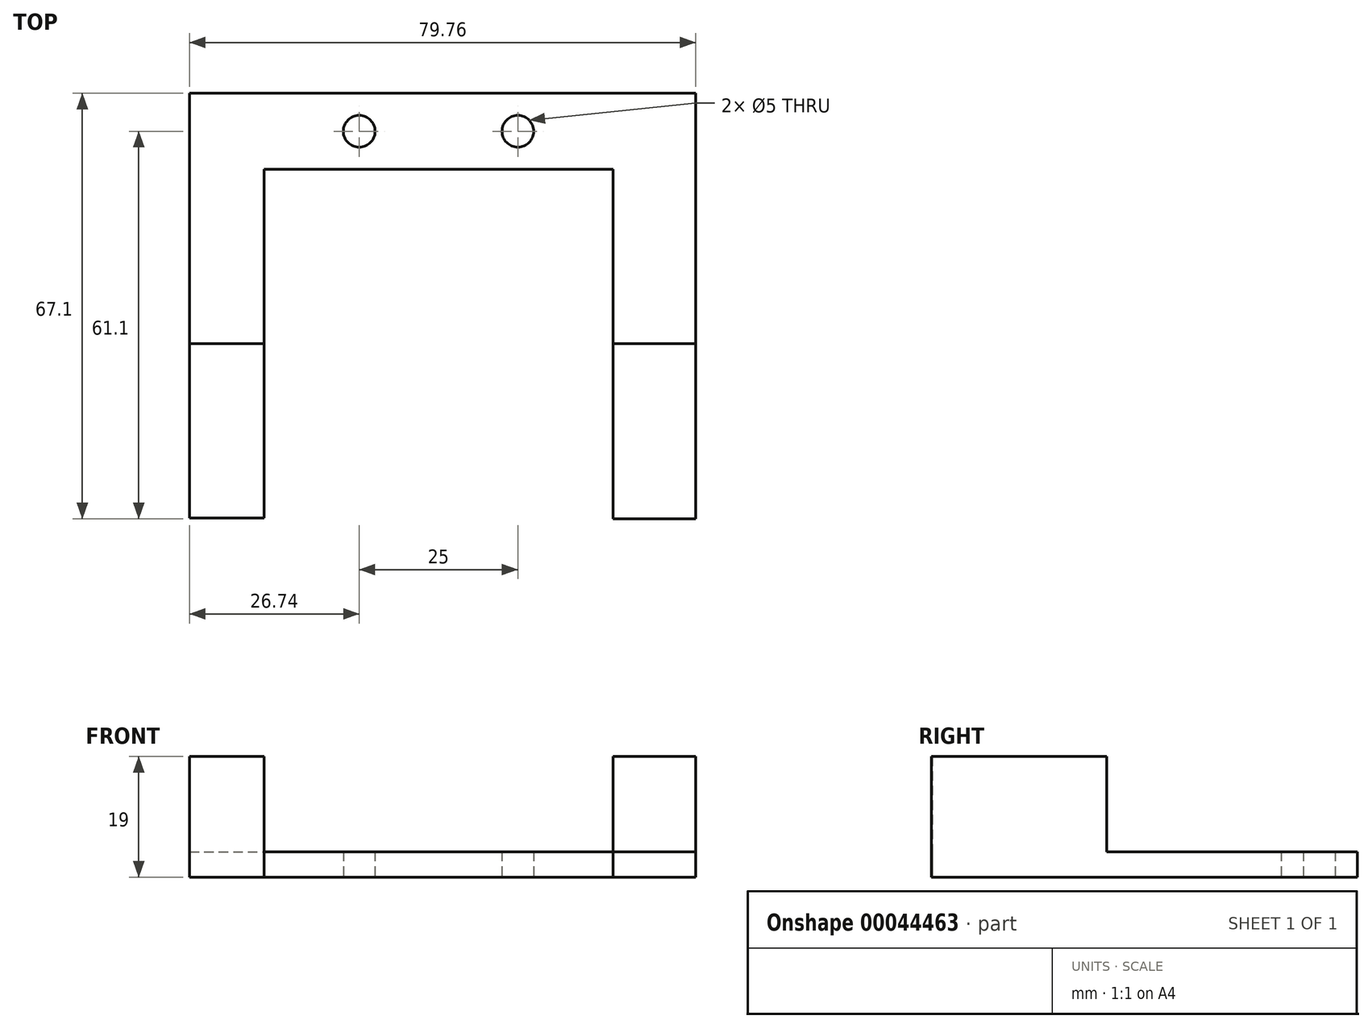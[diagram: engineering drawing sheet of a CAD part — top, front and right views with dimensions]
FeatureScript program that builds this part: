
annotation { "Feature Type Name" : "Feature", "Feature Type Description" : "" }
export const myFeature = defineFeature(function(context is Context, id is Id, definition is map)
    precondition{}
    {
        {
            var Q0;
            Q0=qCreatedBy(makeId("Top.planeOp"),FACE);
            var sketch = newSketch(context, id + "F0", { "sketchPlane" : qUnion([Q0])});
            skLineSegment(sketch, "E0.rect.bottom", {"start": v(27.5, -27.5) * mm, "end": v(-27.5, -27.5) * mm, "construction": true});
            skLineSegment(sketch, "E0.rect.top", {"start": v(27.5, 27.5) * mm, "end": v(-27.5, 27.5) * mm});
            skLineSegment(sketch, "E0.rect.left", {"start": v(27.5, -27.5) * mm, "end": v(27.5, 27.5) * mm});
            skLineSegment(sketch, "E0.rect.right", {"start": v(-27.5, -27.5) * mm, "end": v(-27.5, 27.5) * mm});
            skPoint(sketch, "E0.rect.middle", {"position": v(0, 0) * mm});
            skLineSegment(sketch, "E1", {"start": v(-27.5, -27.5) * mm, "end": v(-39.24, -27.5) * mm});
            skLineSegment(sketch, "E2", {"start": v(-39.24, -27.5) * mm, "end": v(-39.24, 39.5) * mm});
            skLineSegment(sketch, "E3", {"start": v(-39.24, 39.5) * mm, "end": v(40.52, 39.5) * mm});
            skLineSegment(sketch, "E4", {"start": v(40.52, 39.5) * mm, "end": v(40.52, -27.6) * mm});
            skLineSegment(sketch, "E5", {"start": v(27.5, -27.5) * mm, "end": v(40.52, -27.6) * mm});
            skLineSegment(sketch, "E6", {"start": v(-12.5, 0) * mm, "end": v(0, 0) * mm, "construction": true});
            skLineSegment(sketch, "E7", {"start": v(0, 0) * mm, "end": v(12.5, 0) * mm, "construction": true});
            skLineSegment(sketch, "E8", {"start": v(-27.5, 27.5) * mm, "end": v(-27.5, 39.5) * mm, "construction": true});
            skLineSegment(sketch, "E9", {"start": v(-27.5, 33.5) * mm, "end": v(27.8, 33.5) * mm, "construction": true});
            skLineSegment(sketch, "E10", {"start": v(-12.5, 0) * mm, "end": v(-12.5, 33.5) * mm, "construction": true});
            skLineSegment(sketch, "E11", {"start": v(12.5, 0) * mm, "end": v(12.5, 33.5) * mm, "construction": true});
            skCircle(sketch, "E12", {"center": v(-12.5, 33.5) * mm, "radius": 2.5 * mm});
            skCircle(sketch, "E13", {"center": v(12.5, 33.5) * mm, "radius": 2.5 * mm});
            skSolve(sketch);
        }
        {
            var Q0;
            Q0=makeQuery(id+"F0.imprint","IMPRINT",FACE,{"disambiguationData":[TD([[makeQuery(id+"F0.imprint","IMPRINT",EDGE,{"derivedFrom":sQuery(id+"F0.wireOp",EDGE,"E0.rect.top")}),-1.0]])]});
            extrude(context, id + "F1", {"entities" : qUnion([Q0]), "depth" : 4 * mm});
        }
        {
            var Q0;
            Q0=makeQuery(id+"F1.opExtrude","CAP_FACE",FACE,{"disambiguationData":[OSD([sQuery(id+"F0.wireOp",EDGE,"E0.rect.top"),sQuery(id+"F0.wireOp",EDGE,"E0.rect.left"),sQuery(id+"F0.wireOp",EDGE,"E0.rect.right"),sQuery(id+"F0.wireOp",EDGE,"E1"),sQuery(id+"F0.wireOp",EDGE,"E2"),sQuery(id+"F0.wireOp",EDGE,"E3"),sQuery(id+"F0.wireOp",EDGE,"E4"),sQuery(id+"F0.wireOp",EDGE,"E5"),sQuery(id+"F0.wireOp",EDGE,"E12"),sQuery(id+"F0.wireOp",EDGE,"E13")])],"isStart":false});
            var sketch = newSketch(context, id + "F2", { "sketchPlane" : qUnion([Q0])});
            skLineSegment(sketch, "E14.bottom", {"start": v(-39.24, -27.5) * mm, "end": v(-27.5, -27.5) * mm});
            skLineSegment(sketch, "E14.top", {"start": v(-39.24, 0) * mm, "end": v(-27.5, 0) * mm});
            skLineSegment(sketch, "E14.left", {"start": v(-39.24, -27.5) * mm, "end": v(-39.24, 0) * mm});
            skLineSegment(sketch, "E14.right", {"start": v(-27.5, -27.5) * mm, "end": v(-27.5, 0) * mm});
            skLineSegment(sketch, "E15.bottom", {"start": v(27.5, 0) * mm, "end": v(40.52, 0) * mm});
            skLineSegment(sketch, "E15.top", {"start": v(27.5, -27.6) * mm, "end": v(40.52, -27.6) * mm});
            skLineSegment(sketch, "E15.left", {"start": v(27.5, 0) * mm, "end": v(27.5, -27.6) * mm});
            skLineSegment(sketch, "E15.right", {"start": v(40.52, 0) * mm, "end": v(40.52, -27.6) * mm});
            skSolve(sketch);
        }
        {
            var Q0;
            Q0 = qSketchRegion(id + "F2", true);
            extrude(context, id + "F3", {"entities" : qUnion([Q0]), "operationType" : NewBodyOperationType.ADD, "depth" : 15 * mm});
        }
    });
